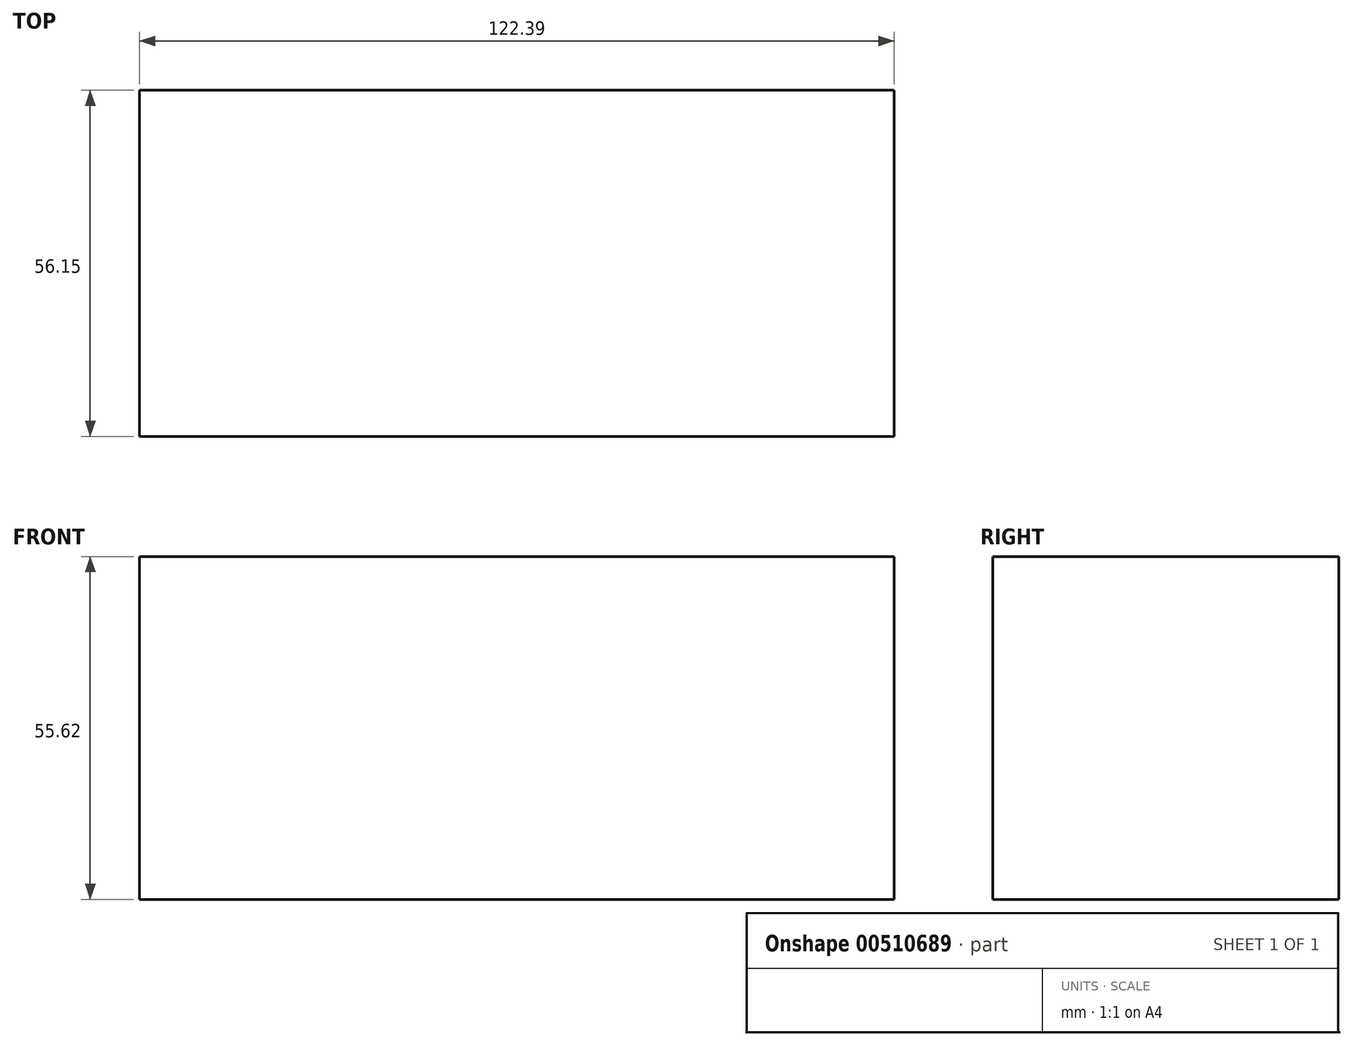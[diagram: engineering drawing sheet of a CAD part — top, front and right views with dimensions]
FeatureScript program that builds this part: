
annotation { "Feature Type Name" : "Feature", "Feature Type Description" : "" }
export const myFeature = defineFeature(function(context is Context, id is Id, definition is map)
    precondition{}
    {
        {
            var Q0;
            Q0=qCreatedBy(makeId("Right.planeOp"),FACE);
            var sketch = newSketch(context, id + "F0", { "sketchPlane" : qUnion([Q0])});
            skLineSegment(sketch, "E0.bottom", {"start": v(41.31, 0) * mm, "end": v(-14.84, 0) * mm});
            skLineSegment(sketch, "E0.top", {"start": v(41.31, -55.62) * mm, "end": v(-14.84, -55.62) * mm});
            skLineSegment(sketch, "E0.left", {"start": v(41.31, 0) * mm, "end": v(41.31, -55.62) * mm});
            skLineSegment(sketch, "E0.right", {"start": v(-14.84, 0) * mm, "end": v(-14.84, -55.62) * mm});
            skSolve(sketch);
        }
        {
            var Q0;
            Q0=makeQuery(id+"F0.imprint","IMPRINT",FACE,{"disambiguationData":[TD([[makeQuery(id+"F0.imprint","IMPRINT",EDGE,{"derivedFrom":sQuery(id+"F0.wireOp",EDGE,"E0.bottom")}),1.0]])]});
            extrude(context, id + "F1", {"entities" : qUnion([Q0]), "depth" : 61.76 * mm});
        }
        {
            var Q0;
            Q0=makeQuery(id+"F1.opExtrude","CAP_FACE",FACE,{"disambiguationData":[OSD([sQuery(id+"F0.wireOp",EDGE,"E0.bottom"),sQuery(id+"F0.wireOp",EDGE,"E0.top"),sQuery(id+"F0.wireOp",EDGE,"E0.left"),sQuery(id+"F0.wireOp",EDGE,"E0.right")])],"isStart":true});
            extrude(context, id + "F2", {"entities" : qUnion([Q0]), "operationType" : NewBodyOperationType.ADD, "depth" : 60.63 * mm});
        }
    });
